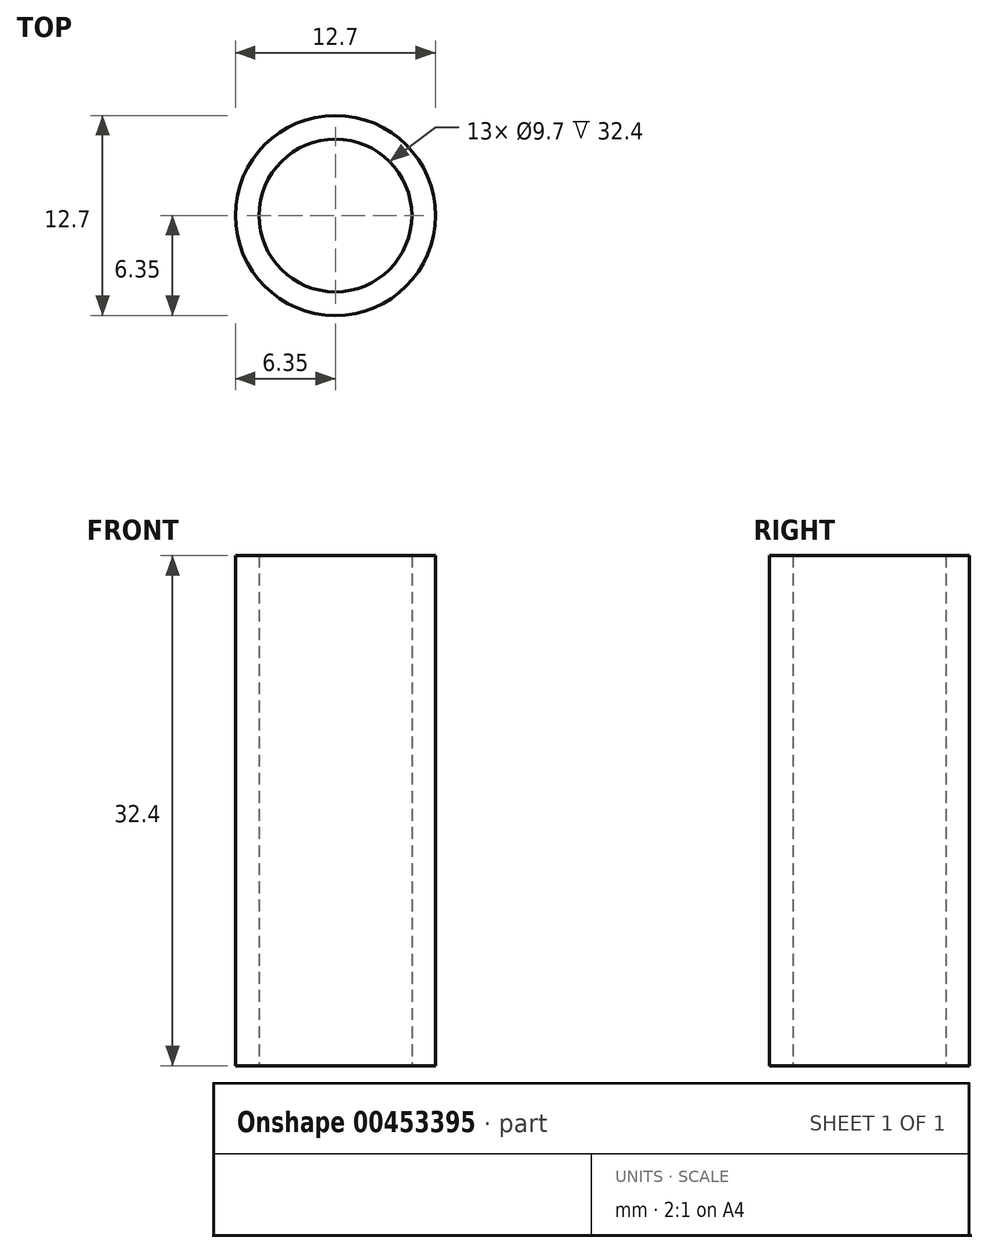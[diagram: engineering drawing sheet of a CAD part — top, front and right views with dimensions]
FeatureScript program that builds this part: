
annotation { "Feature Type Name" : "Feature", "Feature Type Description" : "" }
export const myFeature = defineFeature(function(context is Context, id is Id, definition is map)
    precondition{}
    {
        {
            var Q0;
            Q0=qCreatedBy(makeId("Top.planeOp"),FACE);
            var sketch = newSketch(context, id + "F0", { "sketchPlane" : qUnion([Q0])});
            skCircle(sketch, "E0", {"center": v(0, 0) * mm, "radius": 4.85 * mm});
            skCircle(sketch, "E1", {"center": v(0, 0) * mm, "radius": 6.35 * mm});
            skSolve(sketch);
        }
        {
            var Q0;
            Q0=makeQuery(id+"F0.imprint","IMPRINT",FACE,{"disambiguationData":[TD([[makeQuery(id+"F0.imprint","IMPRINT",EDGE,{"derivedFrom":sQuery(id+"F0.wireOp",EDGE,"E0")}),-1.0]])]});
            var Q1;
            Q1=sQuery(id+"F0.wireOp",EDGE,"E1");
            var Q2;
            Q2=sQuery(id+"F0.wireOp",EDGE,"E0");
            extrude(context, id + "F1", {"entities" : qUnion([Q0]), "surfaceEntities" : qUnion([Q1, Q2]), "depth" : 32.4 * mm});
        }
    });
